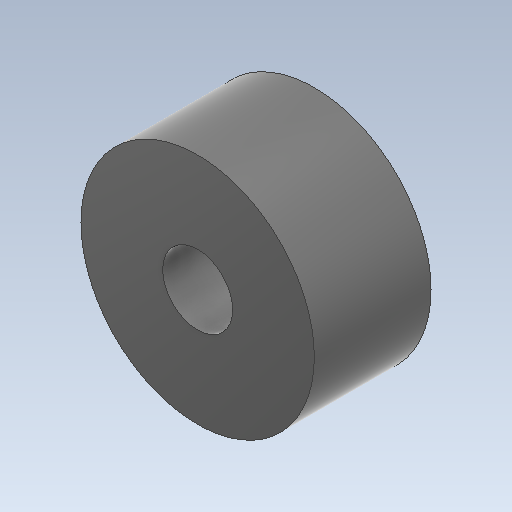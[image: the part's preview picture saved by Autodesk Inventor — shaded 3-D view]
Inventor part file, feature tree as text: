
AUTODESK INVENTOR PART (.ipt)
format: ipt  version: 2020 (Build 240168000, 168)  size: 112,640 bytes
history: native  units: mm
features: sketch x2, extrude x1, hole x1
ambient origin geometry x8: Origin, YZ Plane, XZ Plane, XY Plane, X Axis, Y Axis, Z Axis, Center Point
bodies: Solid1 (feature_tree)
feature tree (4):
  extrude  "Extrusion1"  Depth=5.0mm
  hole  "Hole2"  [1 undecoded]
  sketch  "Sketch1"  dims[d0=20.0mm d1=5.0mm]
  sketch  "Sketch3"  dims[d2=10.0mm d3=0.0mm d11=6.0mm d12=6.0mm d13=13.0mm d14=5.0mm d15=90.0deg d16=8.0mm d17=20.594885mm]
note: 1 required parameter value undecoded (feature->parameter linkage not recoverable at this tier; creation-order binding heuristic only, values carry confidence <= 0.55)
